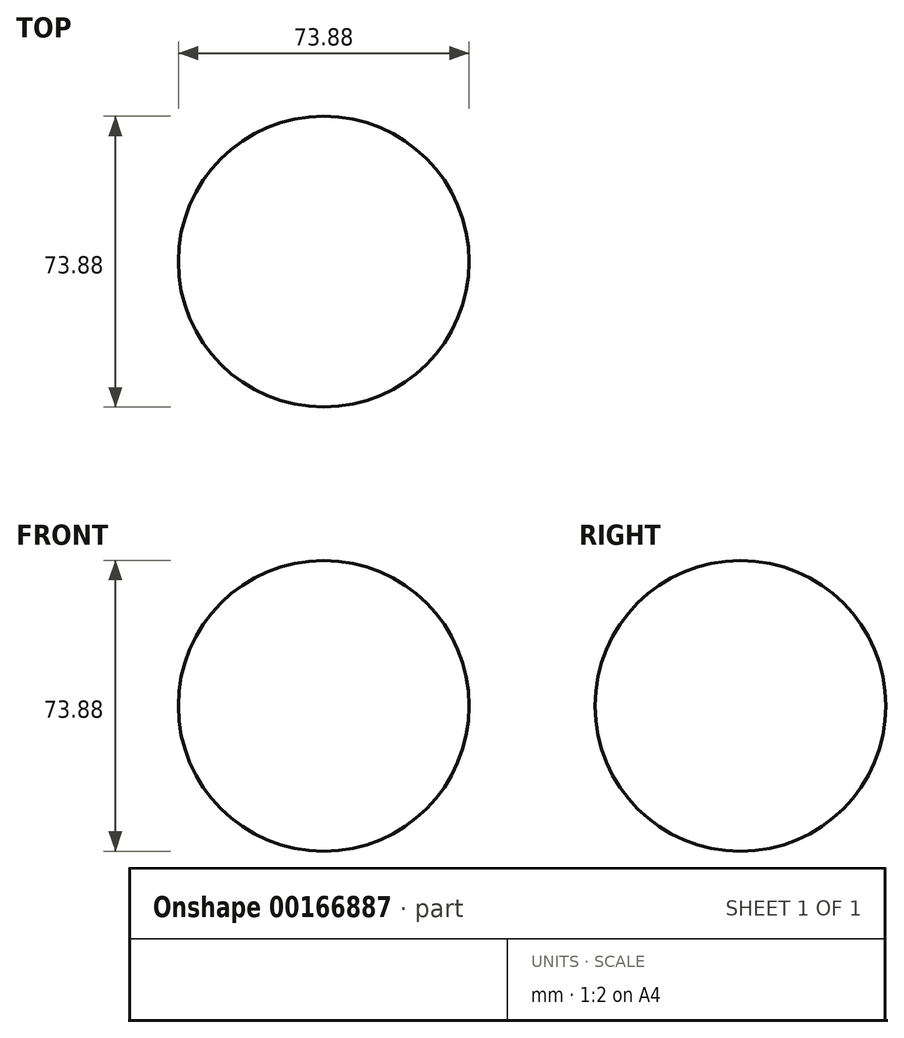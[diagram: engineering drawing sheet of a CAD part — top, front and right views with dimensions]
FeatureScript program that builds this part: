
annotation { "Feature Type Name" : "Feature", "Feature Type Description" : "" }
export const myFeature = defineFeature(function(context is Context, id is Id, definition is map)
    precondition{}
    {
        {
            var Q0;
            Q0=qCreatedBy(makeId("Top.planeOp"),FACE);
            var sketch = newSketch(context, id + "F0", { "sketchPlane" : qUnion([Q0])});
            skArc(sketch, "E0", {"start": v(0, -36.94) * mm, "mid": v(36.94, 0) * mm, "end": v(0, 36.94) * mm});
            skLineSegment(sketch, "E1", {"start": v(0, 36.94) * mm, "end": v(0, -36.94) * mm});
            skSolve(sketch);
        }
        {
            var Q0;
            Q0=makeQuery(id+"F0.imprint","IMPRINT",FACE,{"disambiguationData":[TD([[makeQuery(id+"F0.imprint","IMPRINT",EDGE,{"derivedFrom":sQuery(id+"F0.wireOp",EDGE,"E0")}),1.0]])]});
            var Q1;
            Q1=sQuery(id+"F0.wireOp",EDGE,"E1");
            revolve(context, id + "F1", {"entities" : qUnion([Q0]), "axis" : qUnion([Q1]), "revolveType" : RevolveType.FULL});
        }
    });
